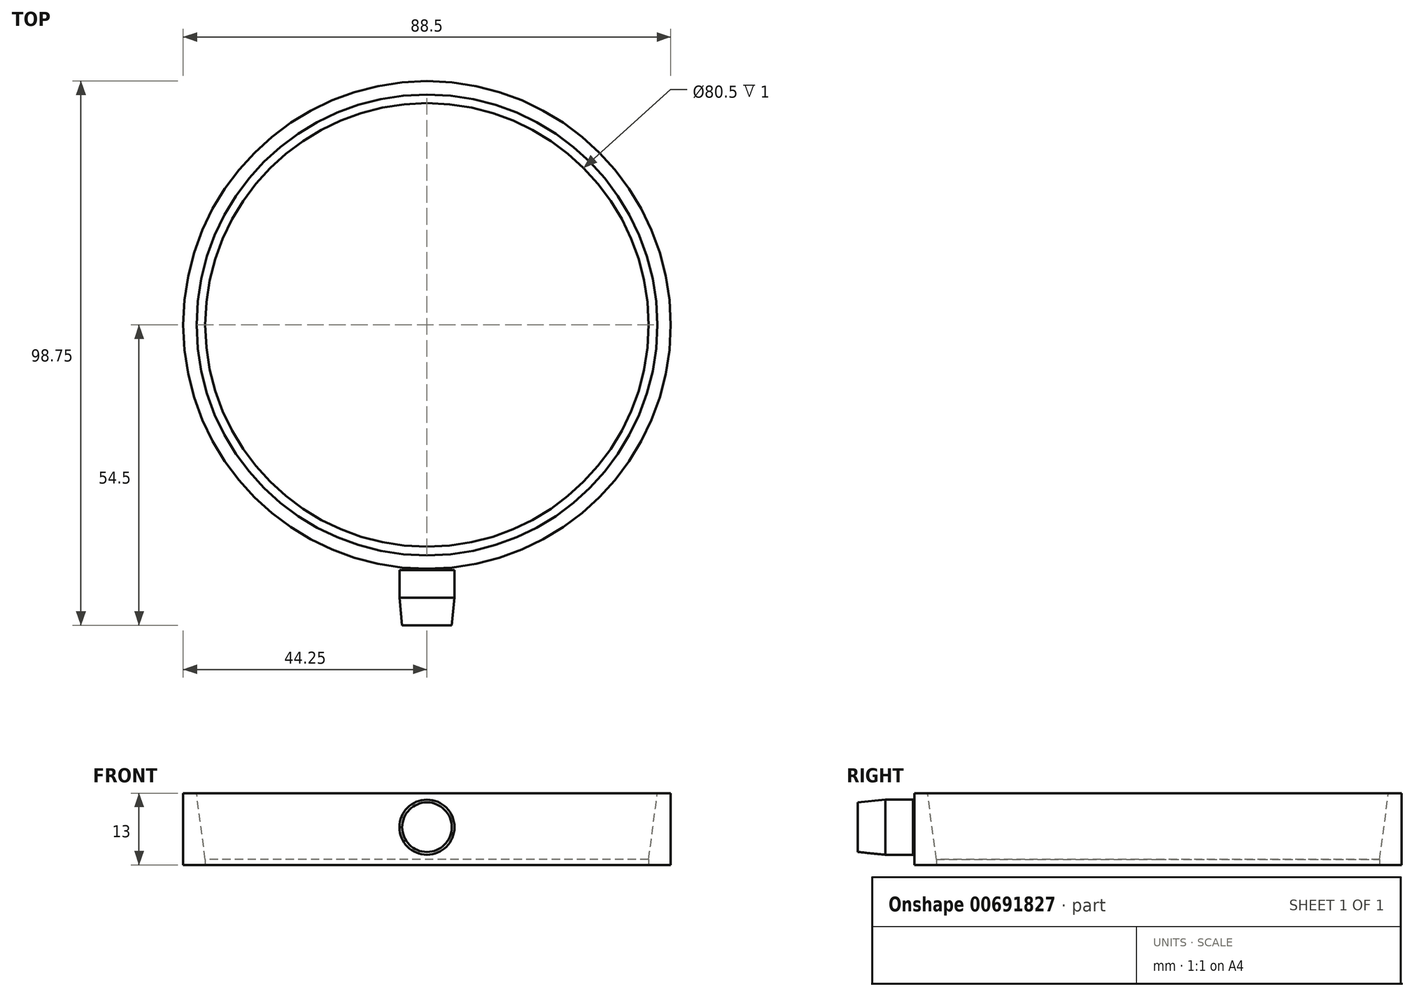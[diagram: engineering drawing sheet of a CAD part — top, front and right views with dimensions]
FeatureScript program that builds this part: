
annotation { "Feature Type Name" : "Feature", "Feature Type Description" : "" }
export const myFeature = defineFeature(function(context is Context, id is Id, definition is map)
    precondition{}
    {
        {
            var Q0;
            Q0=qCreatedBy(makeId("Top.planeOp"),FACE);
            var sketch = newSketch(context, id + "F0", { "sketchPlane" : qUnion([Q0])});
            skCircle(sketch, "E0", {"center": v(0, 0) * mm, "radius": 40.25 * mm});
            skCircle(sketch, "E1.0", {"center": v(0, 0) * mm, "radius": 44.25 * mm});
            skSolve(sketch);
        }
        {
            var Q0;
            Q0=makeQuery(id+"F0.imprint","IMPRINT",FACE,{"disambiguationData":[TD([[makeQuery(id+"F0.imprint","IMPRINT",EDGE,{"derivedFrom":sQuery(id+"F0.wireOp",EDGE,"E0")}),-1.0]])]});
            extrude(context, id + "F1", {"entities" : qUnion([Q0]), "depth" : 13 * mm, "offsetDistance" : 25 * mm});
        }
        {
            var Q0;
            Q0=qCreatedBy(makeId("Front.planeOp"),FACE);
            cPlane(context, id + "F2", {"entities" : qUnion([Q0]), "cplaneType" : CPlaneType.OFFSET, "offset" : 44.5 * mm, "width" : 150 * mm, "height" : 150 * mm});
        }
        {
            var Q0;
            Q0=qCreatedBy(id+"F2.planeOp",FACE);
            var sketch = newSketch(context, id + "F3", { "sketchPlane" : qUnion([Q0])});
            skCircle(sketch, "E2", {"center": v(0, 6.84) * mm, "radius": 5 * mm});
            skSolve(sketch);
        }
        {
            var Q0;
            Q0=qSketchRegion(id+"F3",true);
            extrude(context, id + "F4", {"entities" : qUnion([Q0]), "operationType" : NewBodyOperationType.ADD, "depth" : 10 * mm, "offsetDistance" : 25 * mm});
        }
        {
            var Q0;
            Q0=makeQuery(id+"F1.opExtrude","CAP_EDGE",EDGE,{"disambiguationData":[OSD([sQuery(id+"F0.wireOp",EDGE,"E0")])],"isStart":false});
            chamfer(context, id + "F5", {"entities" : qUnion([Q0]), "chamferType" : ChamferType.OFFSET_ANGLE, "width" : 12 * mm, "oppositeDirection" : false, "angle" : 7.5 * degree, "tangentPropagation" : true});
        }
        {
            var Q0;
            Q0=makeQuery(id+"F4.opExtrude","CAP_EDGE",EDGE,{"disambiguationData":[OSD([sQuery(id+"F3.wireOp",EDGE,"E2")])],"isStart":false});
            chamfer(context, id + "F6", {"entities" : qUnion([Q0]), "chamferType" : ChamferType.TWO_OFFSETS, "width1" : .5 * mm, "oppositeDirection" : false, "width2" : 5 * mm, "tangentPropagation" : true});
        }
    });
